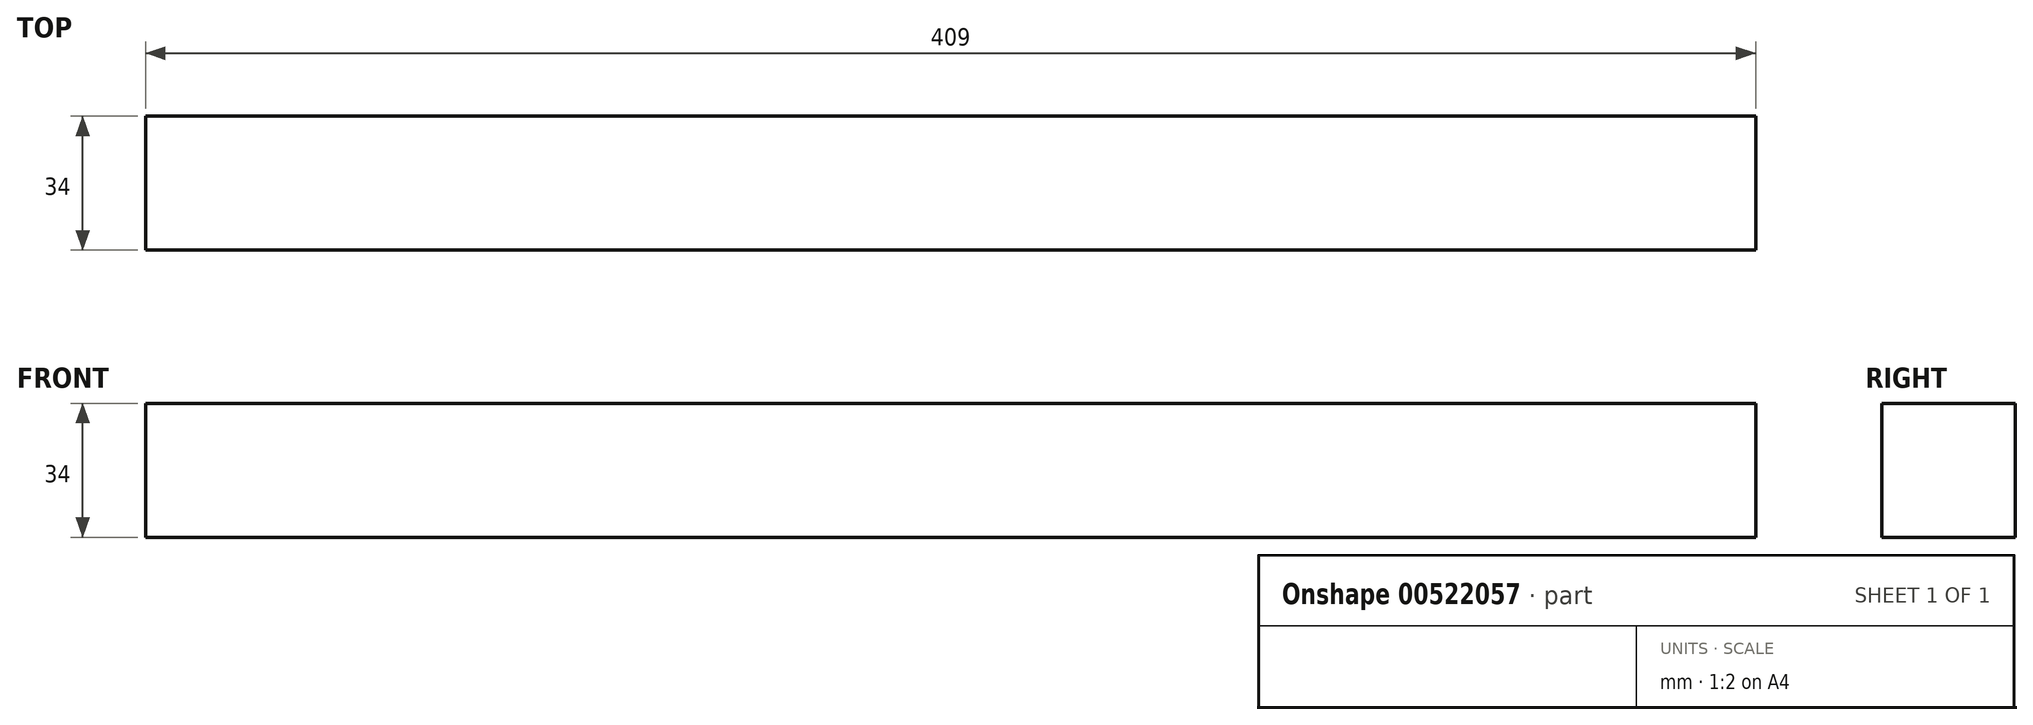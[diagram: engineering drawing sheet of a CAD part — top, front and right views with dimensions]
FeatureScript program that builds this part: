
annotation { "Feature Type Name" : "Feature", "Feature Type Description" : "" }
export const myFeature = defineFeature(function(context is Context, id is Id, definition is map)
    precondition{}
    {
        {
            var Q0;
            Q0=qCreatedBy(makeId("Right.planeOp"),FACE);
            var sketch = newSketch(context, id + "F0", { "sketchPlane" : qUnion([Q0])});
            skLineSegment(sketch, "E0.bottom", {"start": v(0, 0) * mm, "end": v(-34, 0) * mm});
            skLineSegment(sketch, "E0.top", {"start": v(0, 34) * mm, "end": v(-34, 34) * mm});
            skLineSegment(sketch, "E0.left", {"start": v(0, 0) * mm, "end": v(0, 34) * mm});
            skLineSegment(sketch, "E0.right", {"start": v(-34, 0) * mm, "end": v(-34, 34) * mm});
            skSolve(sketch);
        }
        {
            var Q0;
            Q0=makeQuery(id+"F0.imprint","IMPRINT",FACE,{"disambiguationData":[TD([[makeQuery(id+"F0.imprint","IMPRINT",EDGE,{"derivedFrom":sQuery(id+"F0.wireOp",EDGE,"E0.bottom")}),-1.0]])]});
            extrude(context, id + "F1", {"entities" : qUnion([Q0]), "oppositeDirection" : true, "depth" : 409 * mm, "offsetDistance" : 25 * mm});
        }
    });
